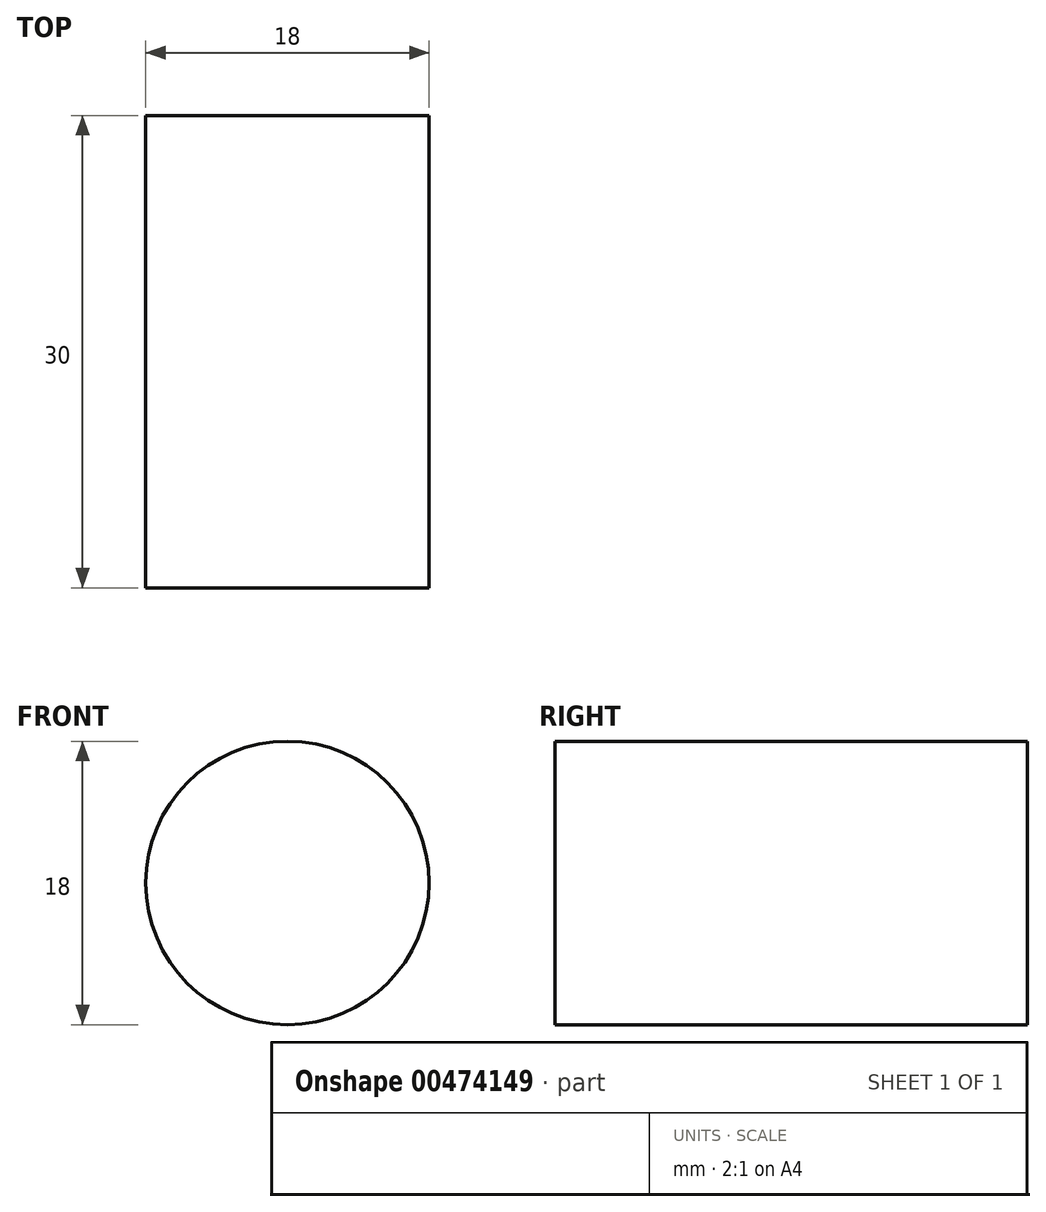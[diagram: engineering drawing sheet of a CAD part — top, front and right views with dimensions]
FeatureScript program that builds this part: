
annotation { "Feature Type Name" : "Feature", "Feature Type Description" : "" }
export const myFeature = defineFeature(function(context is Context, id is Id, definition is map)
    precondition{}
    {
        {
            var Q0;
            Q0=qCreatedBy(makeId("Front.planeOp"),FACE);
            var sketch = newSketch(context, id + "F0", { "sketchPlane" : qUnion([Q0])});
            skCircle(sketch, "E0", {"center": v(0, 0) * mm, "radius": 9 * mm});
            skSolve(sketch);
        }
        {
            var Q0;
            Q0=makeQuery(id+"F0.imprint","IMPRINT",FACE,{"disambiguationData":[TD([[makeQuery(id+"F0.imprint","IMPRINT",EDGE,{"derivedFrom":sQuery(id+"F0.wireOp",EDGE,"E0")}),1.0]])]});
            extrude(context, id + "F1", {"entities" : qUnion([Q0]), "endBound" : BoundingType.SYMMETRIC, "depth" : 30 * mm});
        }
    });
